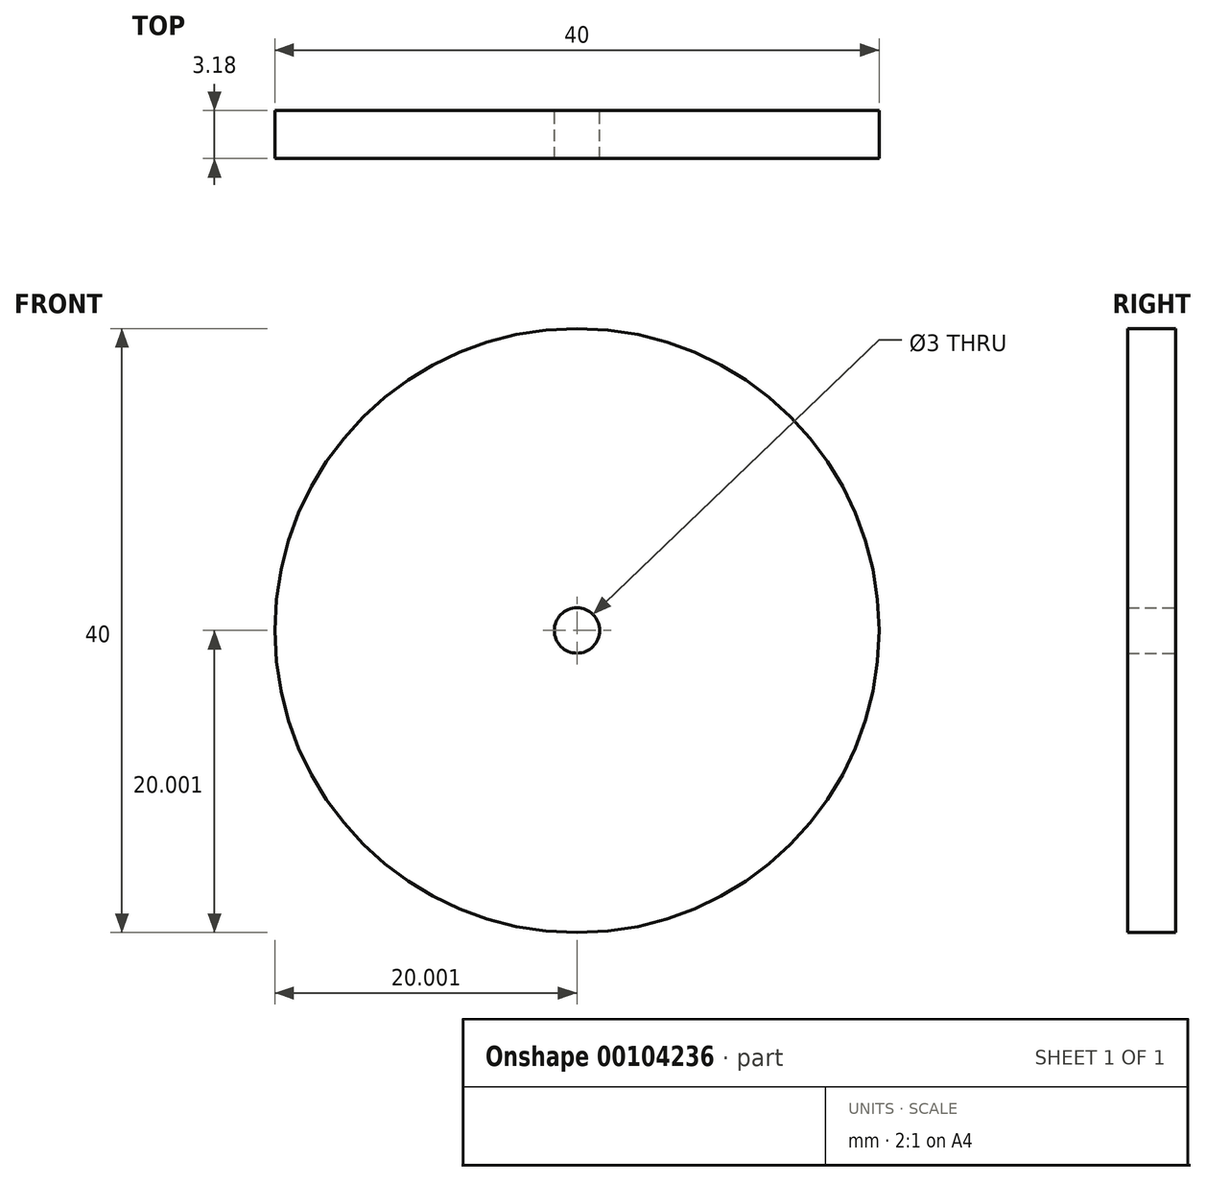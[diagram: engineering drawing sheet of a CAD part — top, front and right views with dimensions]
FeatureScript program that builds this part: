
annotation { "Feature Type Name" : "Feature", "Feature Type Description" : "" }
export const myFeature = defineFeature(function(context is Context, id is Id, definition is map)
    precondition{}
    {
        {
            var Q0;
            Q0=qCreatedBy(makeId("Front.planeOp"),FACE);
            var sketch = newSketch(context, id + "F0", { "sketchPlane" : qUnion([Q0])});
            skCircle(sketch, "E0", {"center": v(-67.76, 38.87) * mm, "radius": 20 * mm});
            skCircle(sketch, "E1", {"center": v(-67.76, 38.87) * mm, "radius": 1.5 * mm});
            skSolve(sketch);
        }
        {
            var Q0;
            Q0=makeQuery(id+"F0.imprint","IMPRINT",FACE,{"disambiguationData":[TD([[makeQuery(id+"F0.imprint","IMPRINT",EDGE,{"derivedFrom":sQuery(id+"F0.wireOp",EDGE,"E0")}),1.0]])]});
            extrude(context, id + "F1", {"entities" : qUnion([Q0]), "depth" : 3.17 * mm});
        }
    });
